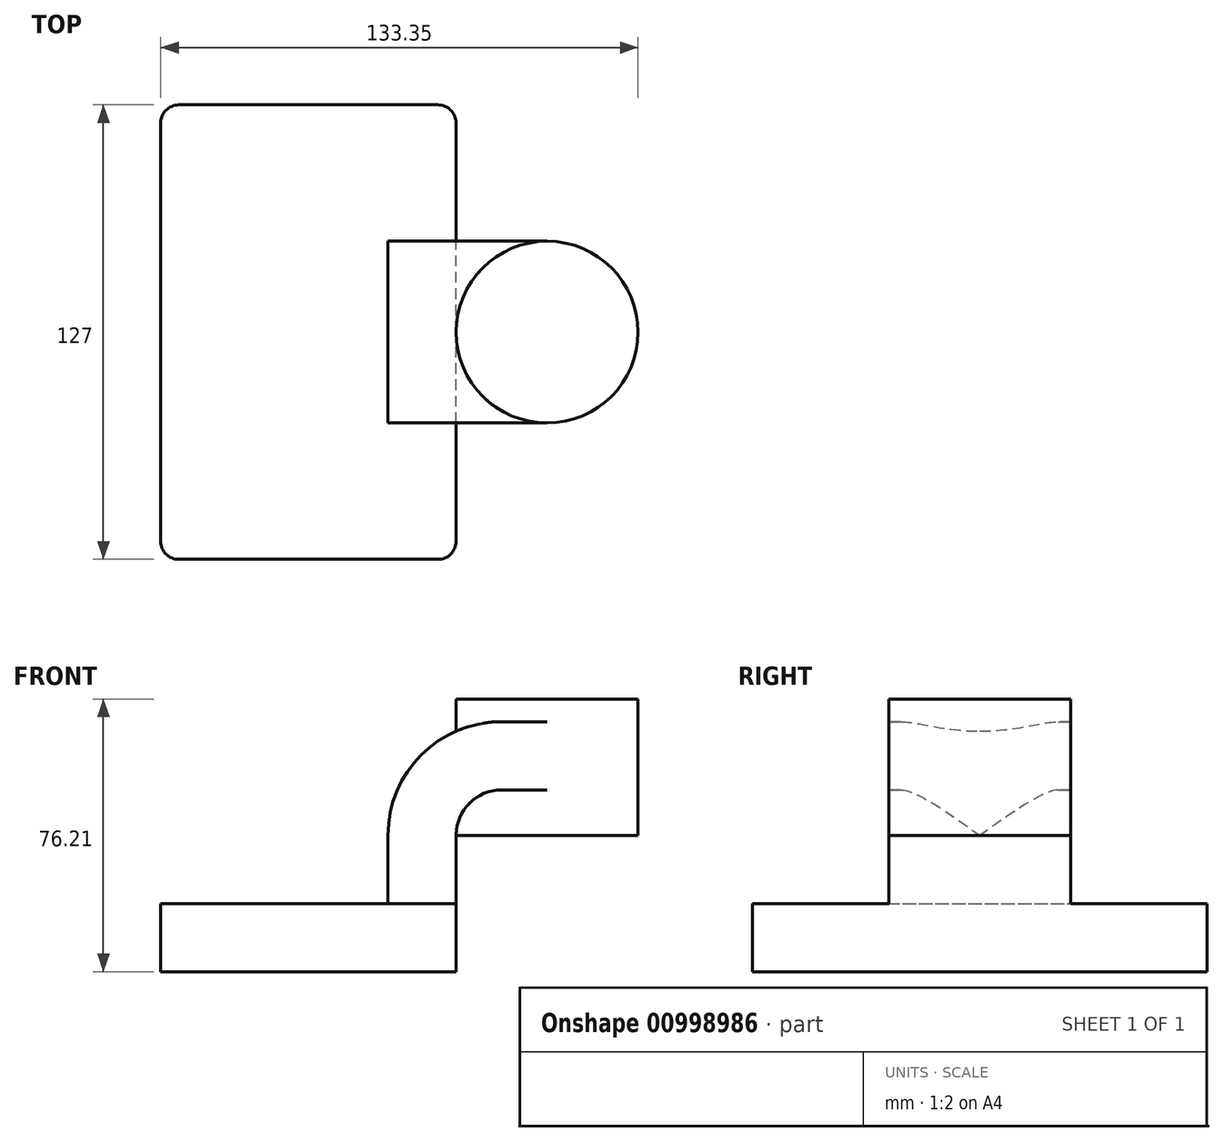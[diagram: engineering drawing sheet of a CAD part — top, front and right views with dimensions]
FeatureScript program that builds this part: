
annotation { "Feature Type Name" : "Feature", "Feature Type Description" : "" }
export const myFeature = defineFeature(function(context is Context, id is Id, definition is map)
    precondition{}
    {
        {
            var Q0;
            Q0=qCreatedBy(makeId("Front.planeOp"),FACE);
            var sketch = newSketch(context, id + "F0", { "sketchPlane" : qUnion([Q0])});
            skLineSegment(sketch, "E0.bottom", {"start": v(-41.28, -9.53) * mm, "end": v(41.28, -9.53) * mm});
            skLineSegment(sketch, "E0.top", {"start": v(-41.28, 9.53) * mm, "end": v(41.28, 9.53) * mm});
            skLineSegment(sketch, "E0.left", {"start": v(-41.28, -9.53) * mm, "end": v(-41.28, 9.53) * mm});
            skLineSegment(sketch, "E0.right", {"start": v(41.28, -9.53) * mm, "end": v(41.28, 9.53) * mm});
            skPoint(sketch, "E0.middle", {"position": v(0, 0) * mm});
            skLineSegment(sketch, "E1.bottom", {"start": v(66.68, 28.58) * mm, "end": v(92.08, 28.58) * mm});
            skLineSegment(sketch, "E1.top", {"start": v(66.67, 66.68) * mm, "end": v(92.08, 66.68) * mm});
            skLineSegment(sketch, "E1.left", {"start": v(66.68, 28.58) * mm, "end": v(66.68, 66.68) * mm});
            skLineSegment(sketch, "E1.right", {"start": v(92.08, 28.58) * mm, "end": v(92.08, 66.68) * mm});
            skPoint(sketch, "E1.middle", {"position": v(79.38, 47.63) * mm});
            skLineSegment(sketch, "E2", {"start": v(41.27, 9.53) * mm, "end": v(41.27, 28.58) * mm});
            skArc(sketch, "E3", {"start": v(41.27, 28.58) * mm, "mid": v(45, 37.56) * mm, "end": v(53.98, 41.28) * mm});
            skLineSegment(sketch, "E4", {"start": v(53.98, 41.28) * mm, "end": v(79.38, 41.28) * mm});
            skLineSegment(sketch, "E5.0", {"start": v(53.98, 60.33) * mm, "end": v(79.38, 60.33) * mm});
            skArc(sketch, "E5.1", {"start": v(22.23, 28.58) * mm, "mid": v(31.52, 51.03) * mm, "end": v(53.98, 60.33) * mm});
            skLineSegment(sketch, "E5.2", {"start": v(22.22, 9.53) * mm, "end": v(22.22, 28.58) * mm});
            skLineSegment(sketch, "E6", {"start": v(79.38, 66.68) * mm, "end": v(79.38, 28.58) * mm});
            skFitSpline(sketch, "E7", {"points": [v(-41.28, 9.53) * mm, v(53.98, 60.33) * mm], "startDerivative": vector(0.72, 69.58) * mm, "endDerivative": vector(122.33, 0.06) * mm});
            skSolve(sketch);
        }
        {
            var Q0;
            Q0=makeQuery(id+"F0.imprint","IMPRINT",FACE,{"disambiguationData":[TD([[makeQuery(id+"F0.imprint","IMPRINT",EDGE,{"derivedFrom":sQuery(id+"F0.wireOp",EDGE,"E0.bottom")}),1.0]])]});
            extrude(context, id + "F1", {"entities" : qUnion([Q0]), "endBound" : BoundingType.SYMMETRIC, "depth" : 127 * mm, "offsetDistance" : 25.4 * mm});
        }
        {
            var Q0;
            {var subQ1=sQuery(id+"F0.wireOp",EDGE,"E2");Q0=makeQuery(id+"F0.imprint","IMPRINT",FACE,{"disambiguationData":[TD([[makeQuery(id+"F0.imprint","IMPRINT",EDGE,{"derivedFrom":subQ1}),1.0]])]});}
            extrude(context, id + "F2", {"entities" : qUnion([Q0]), "operationType" : NewBodyOperationType.ADD, "endBound" : BoundingType.SYMMETRIC, "depth" : 50.8 * mm, "offsetDistance" : 25.4 * mm});
        }
        {
            var Q0;
            Q0=makeQuery(id+"F0.imprint","IMPRINT",FACE,{"disambiguationData":[TD([[makeQuery(id+"F0.imprint","IMPRINT",EDGE,{"derivedFrom":sQuery(id+"F0.wireOp",EDGE,"E5.1")}),1.0]])]});
            extrude(context, id + "F3", {"entities" : qUnion([Q0]), "operationType" : NewBodyOperationType.ADD, "endBound" : BoundingType.SYMMETRIC, "depth" : 15.24 * mm, "offsetDistance" : 25.4 * mm});
        }
        {
            var Q0;
            {var subQ0=sQuery(id+"F0.wireOp",EDGE,"E1.right");Q0=makeQuery(id+"F0.imprint","IMPRINT",FACE,{"disambiguationData":[TD([[makeQuery(id+"F0.imprint","IMPRINT",EDGE,{"derivedFrom":subQ0}),1.0]])]});}
            var Q1;
            {var subQ0=sQuery(id+"F0.wireOp",EDGE,"E1.left");var subQ1=sQuery(id+"F0.wireOp",EDGE,"E1.top");var subQ2=makeQuery(id+"F0.imprint","INTERSECT",VERTEX,{"derivedFrom":[subQ1,subQ0]});Q1=makeQuery(id+"F0.imprint","IMPRINT",FACE,{"disambiguationData":[TD([[makeQuery(id+"F0.imprint","IMPRINT",EDGE,{"disambiguationData":[TD([[subQ2,-1.0]])],"derivedFrom":subQ1}),-1.0]])]});}
            var Q2;
            {var subQ0=sQuery(id+"F0.wireOp",EDGE,"E4");var subQ1=sQuery(id+"F0.wireOp",EDGE,"E1.left");var subQ2=makeQuery(id+"F0.imprint","INTERSECT",VERTEX,{"derivedFrom":[subQ1,subQ0]});Q2=makeQuery(id+"F0.imprint","IMPRINT",FACE,{"disambiguationData":[TD([[makeQuery(id+"F0.imprint","IMPRINT",EDGE,{"disambiguationData":[TD([[subQ2,-1.0]])],"derivedFrom":subQ1}),-1.0]])]});}
            var Q3;
            {var subQ0=sQuery(id+"F0.wireOp",EDGE,"E1.left");var subQ1=sQuery(id+"F0.wireOp",EDGE,"E1.bottom");var subQ2=makeQuery(id+"F0.imprint","INTERSECT",VERTEX,{"derivedFrom":[subQ1,subQ0]});Q3=makeQuery(id+"F0.imprint","IMPRINT",FACE,{"disambiguationData":[TD([[makeQuery(id+"F0.imprint","IMPRINT",EDGE,{"disambiguationData":[TD([[subQ2,-1.0]])],"derivedFrom":subQ1}),1.0]])]});}
            var Q4;
            Q4=sQuery(id+"F0.wireOp",EDGE,"E1.left");
            revolve(context, id + "F4", {"operationType" : NewBodyOperationType.ADD, "surfaceOperationType" : NewSurfaceOperationType.NEW, "entities" : qUnion([Q0, Q1, Q2, Q3]), "axis" : qUnion([Q4]), "revolveType" : RevolveType.FULL});
        }
        {
            var Q0;
            Q0=makeQuery(id+"F1.opExtrude","CAP_EDGE",EDGE,{"disambiguationData":[OSD([sQuery(id+"F0.wireOp",EDGE,"E0.right")])],"isStart":false});
            var Q1;
            Q1=makeQuery(id+"F1.opExtrude","CAP_EDGE",EDGE,{"disambiguationData":[OSD([sQuery(id+"F0.wireOp",EDGE,"E0.right")])],"isStart":true});
            var Q2;
            Q2=makeQuery(id+"F1.opExtrude","CAP_EDGE",EDGE,{"disambiguationData":[OSD([sQuery(id+"F0.wireOp",EDGE,"E0.left")])],"isStart":true});
            var Q3;
            Q3=makeQuery(id+"F1.opExtrude","CAP_EDGE",EDGE,{"disambiguationData":[OSD([sQuery(id+"F0.wireOp",EDGE,"E0.left")])],"isStart":false});
            fillet(context, id + "F5", {"entities" : qUnion([Q0, Q1, Q2, Q3]), "radius" : 5.08 * mm, "tangentPropagation" : true, "allowEdgeOverflow" : false});
        }
    });
